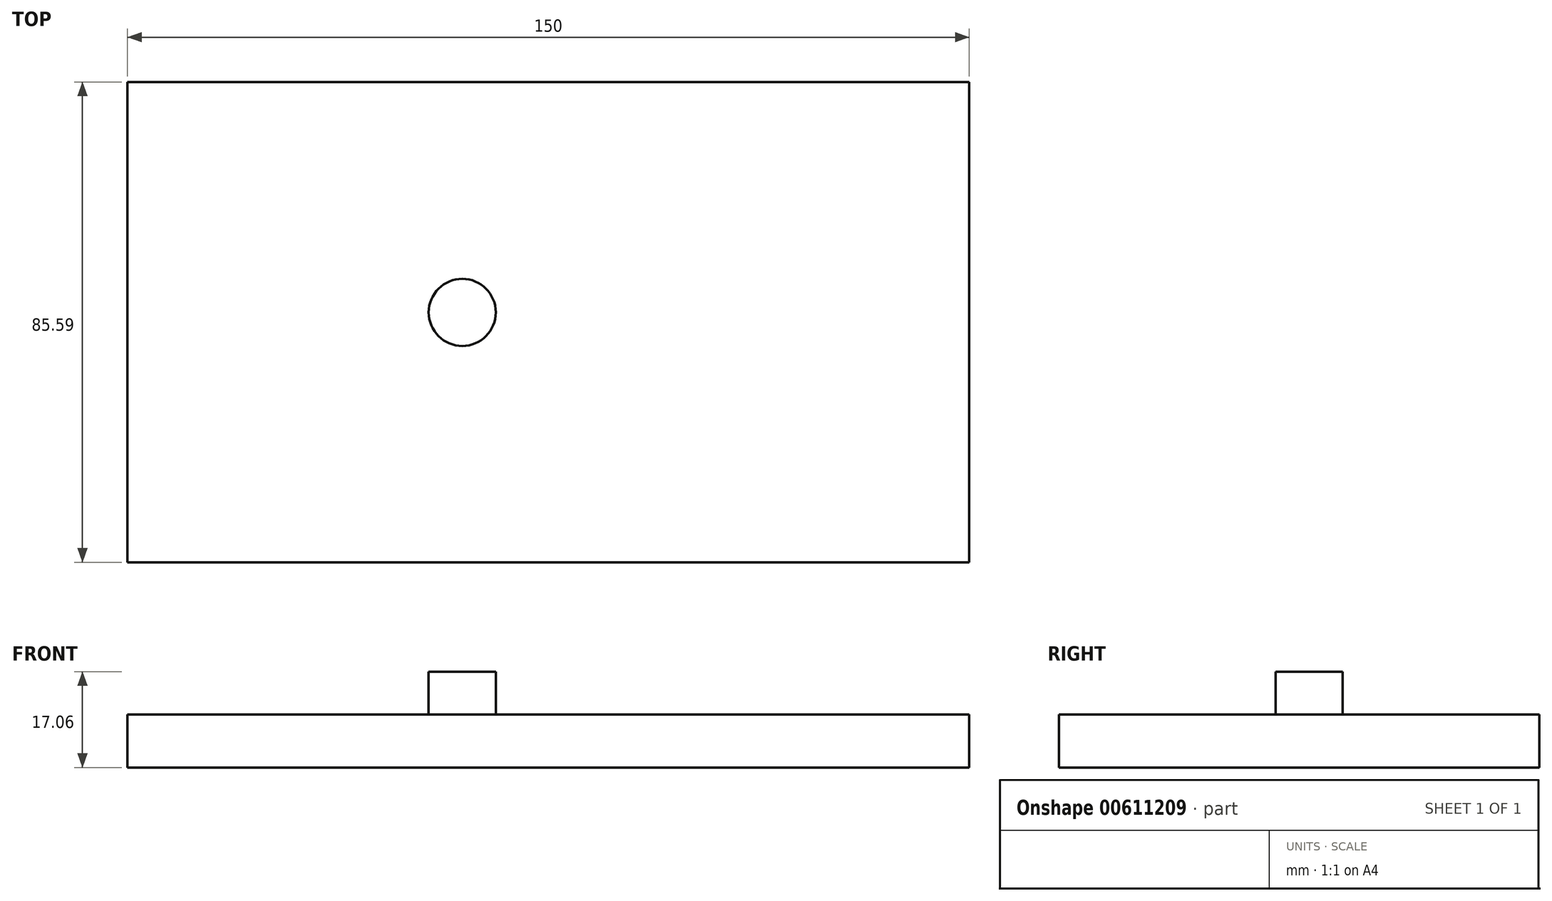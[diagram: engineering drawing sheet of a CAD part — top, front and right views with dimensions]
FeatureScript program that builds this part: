
annotation { "Feature Type Name" : "Feature", "Feature Type Description" : "" }
export const myFeature = defineFeature(function(context is Context, id is Id, definition is map)
    precondition{}
    {
        {
            var Q0;
            Q0=qCreatedBy(makeId("Right.planeOp"),FACE);
            var sketch = newSketch(context, id + "F0", { "sketchPlane" : qUnion([Q0])});
            skLineSegment(sketch, "E0.bottom", {"start": v(-72.26, 9.44) * mm, "end": v(13.33, 9.44) * mm});
            skLineSegment(sketch, "E0.top", {"start": v(-72.26, 0) * mm, "end": v(13.33, 0) * mm});
            skLineSegment(sketch, "E0.left", {"start": v(-72.26, 9.44) * mm, "end": v(-72.26, 0) * mm});
            skLineSegment(sketch, "E0.right", {"start": v(13.33, 9.44) * mm, "end": v(13.33, 0) * mm});
            skSolve(sketch);
        }
        {
            var Q0;
            Q0 = qSketchRegion(id + "F0", true);
            extrude(context, id + "F1", {"entities" : qUnion([Q0]), "depth" : 150 * mm, "offsetDistance" : 25.4 * mm});
        }
        {
            var Q0;
            Q0=makeQuery(id+"F1.opExtrude","SWEPT_FACE",FACE,{"disambiguationData":[OSD([sQuery(id+"F0.wireOp",EDGE,"E0.left")])]});
            extrude(context, id + "F2", {"entities" : qUnion([Q0]), "operationType" : NewBodyOperationType.REMOVE, "depth" : 150 * mm, "offsetDistance" : 25.4 * mm});
        }
        {
            var Q0;
            {var subQ0=sQuery(id+"F0.wireOp",EDGE,"E0.left");var subQ1=makeQuery(id+"F1.opExtrude","CAP_EDGE",EDGE,{"disambiguationData":[OSD([subQ0])],"isStart":false});var subQ2=makeQuery(id+"F2.opExtrude","CAP_EDGE",EDGE,{"disambiguationData":[OSD([subQ0]),TDD([subQ1])],"isStart":false});Q0=makeQuery(id+"FTHGv5wTm0b719A_1.boolean.opBoolean","MERGE",FACE,{"derivedFrom":[makeQuery(id+"FGU4AfDuUkTrhIF_1.boolean.opBoolean","MERGE",FACE,{"derivedFrom":[makeQuery(id+"F2.boolean.opBoolean","MERGE",FACE,{"derivedFrom":[makeQuery(id+"F1.opExtrude","CAP_FACE",FACE,{"disambiguationData":[OSD([sQuery(id+"F0.wireOp",EDGE,"E0.bottom"),sQuery(id+"F0.wireOp",EDGE,"E0.top"),subQ0,sQuery(id+"F0.wireOp",EDGE,"E0.right")])],"isStart":false}),makeQuery(id+"F2.opExtrude","SWEPT_FACE",FACE,{"disambiguationData":[OSD([subQ0]),TDD([subQ1])]})]}),makeQuery(id+"FGU4AfDuUkTrhIF_1.opExtrude","SWEPT_FACE",FACE,{"disambiguationData":[OSD([subQ0]),TDD([subQ2])]})]}),makeQuery(id+"FTHGv5wTm0b719A_1.opExtrude","SWEPT_FACE",FACE,{"disambiguationData":[OSD([subQ0]),TDD([makeQuery(id+"FGU4AfDuUkTrhIF_1.opExtrude","CAP_EDGE",EDGE,{"disambiguationData":[OSD([subQ0]),TDD([subQ2])],"isStart":false})])]})]});}
            extrude(context, id + "F3", {"entities" : qUnion([Q0]), "operationType" : NewBodyOperationType.REMOVE, "depth" : 150 * mm, "offsetDistance" : 25.4 * mm});
        }
        {
            var Q0;
            {var subQ0=sQuery(id+"F0.wireOp",EDGE,"E0.left");var subQ1=sQuery(id+"F0.wireOp",EDGE,"E0.bottom");Q0=makeQuery(id+"F3.boolean.opBoolean","MERGE",FACE,{"derivedFrom":[makeQuery(id+"FTHGv5wTm0b719A_1.boolean.opBoolean","MERGE",FACE,{"derivedFrom":[makeQuery(id+"FGU4AfDuUkTrhIF_1.boolean.opBoolean","MERGE",FACE,{"derivedFrom":[makeQuery(id+"F2.boolean.opBoolean","MERGE",FACE,{"derivedFrom":[makeQuery(id+"F1.opExtrude","SWEPT_FACE",FACE,{"disambiguationData":[OSD([subQ1])]}),makeQuery(id+"F2.opExtrude","SWEPT_FACE",FACE,{"disambiguationData":[OSD([subQ1,subQ0])]})]}),makeQuery(id+"FGU4AfDuUkTrhIF_1.opExtrude","SWEPT_FACE",FACE,{"disambiguationData":[OSD([subQ1,subQ0])]})]}),makeQuery(id+"FTHGv5wTm0b719A_1.opExtrude","SWEPT_FACE",FACE,{"disambiguationData":[OSD([subQ1,subQ0])]})]}),makeQuery(id+"F3.opExtrude","SWEPT_FACE",FACE,{"disambiguationData":[OSD([subQ1,subQ0])]})]});}
            var sketch = newSketch(context, id + "F4", { "sketchPlane" : qUnion([Q0])});
            skCircle(sketch, "E1", {"center": v(59.66, -27.72) * mm, "radius": 5.98 * mm});
            skSolve(sketch);
        }
        {
            var Q0;
            Q0 = qSketchRegion(id + "F4", true);
            extrude(context, id + "F5", {"entities" : qUnion([Q0]), "operationType" : NewBodyOperationType.ADD, "depth" : 7.62 * mm, "offsetDistance" : 25.4 * mm});
        }
    });
